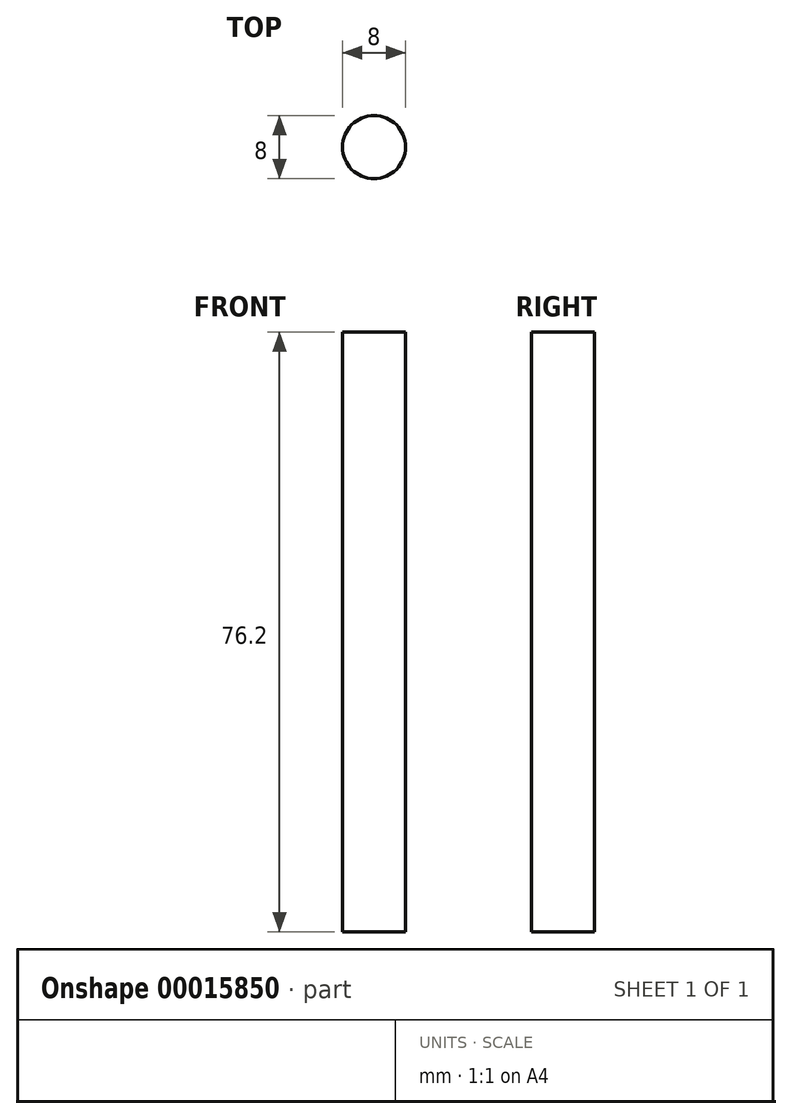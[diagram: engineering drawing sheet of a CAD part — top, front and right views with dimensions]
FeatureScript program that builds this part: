
annotation { "Feature Type Name" : "Feature", "Feature Type Description" : "" }
export const myFeature = defineFeature(function(context is Context, id is Id, definition is map)
    precondition{}
    {
        {
            var Q0;
            Q0=qCreatedBy(makeId("Top.planeOp"),FACE);
            var sketch = newSketch(context, id + "F0", { "sketchPlane" : qUnion([Q0])});
            skCircle(sketch, "E0", {"center": v(0, 0) * mm, "radius": 4 * mm});
            skSolve(sketch);
        }
        {
            var Q0;
            Q0=qSketchRegion(id+"F0",true);
            extrude(context, id + "F1", {"entities" : qUnion([Q0]), "depth" : 76.2 * mm});
        }
    });
